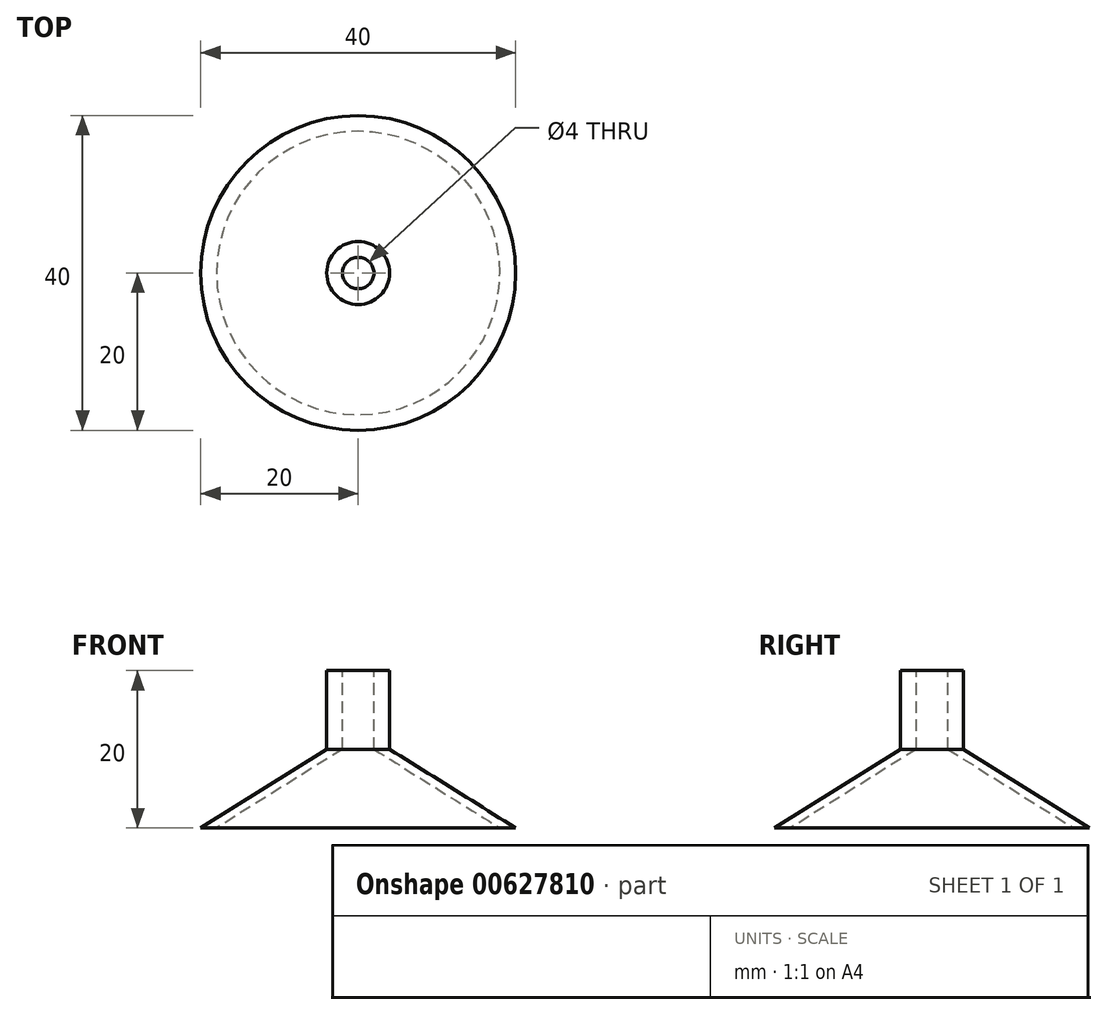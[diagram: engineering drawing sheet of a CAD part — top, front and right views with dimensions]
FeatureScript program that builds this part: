
annotation { "Feature Type Name" : "Feature", "Feature Type Description" : "" }
export const myFeature = defineFeature(function(context is Context, id is Id, definition is map)
    precondition{}
    {
        {
            var Q0;
            Q0=qCreatedBy(makeId("Front.planeOp"),FACE);
            var sketch = newSketch(context, id + "F0", { "sketchPlane" : qUnion([Q0])});
            skLineSegment(sketch, "E0", {"start": v(2, 0) * mm, "end": v(4, 0) * mm});
            skLineSegment(sketch, "E1", {"start": v(0, 20.2) * mm, "end": v(0, 0) * mm, "construction": true});
            skLineSegment(sketch, "E2.MirrorCS", {"start": v(4, 0) * mm, "end": v(4, -10) * mm});
            skLineSegment(sketch, "E3.MirrorCS", {"start": v(2, 0) * mm, "end": v(2, -10) * mm});
            skLineSegment(sketch, "E4.MirrorCS", {"start": v(2, -10) * mm, "end": v(18, -20) * mm});
            skLineSegment(sketch, "E5.MirrorCS", {"start": v(2, -20) * mm, "end": v(18, -20) * mm, "construction": true});
            skLineSegment(sketch, "E6.MirrorCS", {"start": v(2, -10) * mm, "end": v(2, -20) * mm, "construction": true});
            skLineSegment(sketch, "E7.MirrorCS", {"start": v(20, -20) * mm, "end": v(4, -10) * mm});
            skLineSegment(sketch, "E8.MirrorCS", {"start": v(18, -20) * mm, "end": v(20, -20) * mm});
            skSolve(sketch);
        }
        {
            var Q0;
            Q0=makeQuery(id+"F0.imprint","IMPRINT",FACE,{"disambiguationData":[TD([[makeQuery(id+"F0.imprint","IMPRINT",EDGE,{"derivedFrom":sQuery(id+"F0.wireOp",EDGE,"E0")}),-1.0]])]});
            var Q1;
            Q1=sQuery(id+"F0.wireOp",EDGE,"E1");
            revolve(context, id + "F1", {"entities" : qUnion([Q0]), "axis" : qUnion([Q1]), "revolveType" : RevolveType.FULL});
        }
    });
